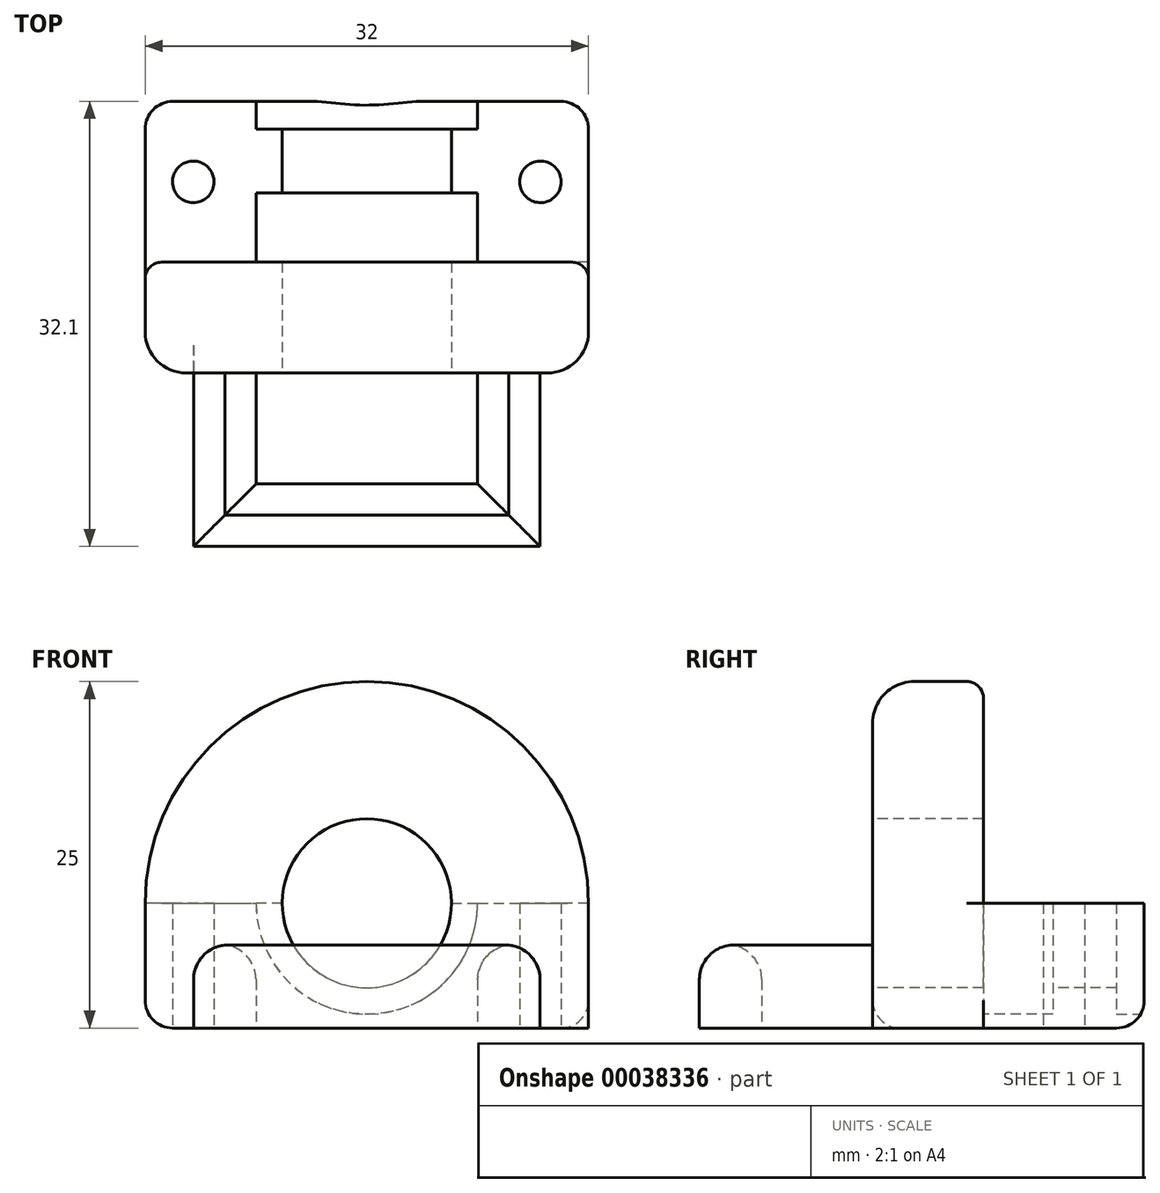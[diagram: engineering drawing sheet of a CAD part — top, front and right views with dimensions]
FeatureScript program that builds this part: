
annotation { "Feature Type Name" : "Feature", "Feature Type Description" : "" }
export const myFeature = defineFeature(function(context is Context, id is Id, definition is map)
    precondition{}
    {
        {
            var Q0;
            Q0=qCreatedBy(makeId("Top.planeOp"),FACE);
            var sketch = newSketch(context, id + "F0", { "sketchPlane" : qUnion([Q0])});
            skLineSegment(sketch, "E0.rect.bottom", {"start": v(-16, 5.8) * mm, "end": v(16, 5.8) * mm});
            skLineSegment(sketch, "E0.rect.top", {"start": v(-16, -5.8) * mm, "end": v(16, -5.8) * mm});
            skLineSegment(sketch, "E0.rect.left", {"start": v(-16, 5.8) * mm, "end": v(-16, -5.8) * mm});
            skLineSegment(sketch, "E0.rect.right", {"start": v(16, 5.8) * mm, "end": v(16, -5.8) * mm});
            skPoint(sketch, "E0.rect.middle", {"position": v(0, 0) * mm});
            skCircle(sketch, "E1", {"center": v(12.52, 0) * mm, "radius": 1.5 * mm});
            skCircle(sketch, "E2", {"center": v(-12.52, 0) * mm, "radius": 1.5 * mm});
            skSolve(sketch);
        }
        {
            var Q0;
            Q0=makeQuery(id+"F0.imprint","IMPRINT",FACE,{"disambiguationData":[TD([[makeQuery(id+"F0.imprint","IMPRINT",EDGE,{"derivedFrom":sQuery(id+"F0.wireOp",EDGE,"E0.rect.bottom")}),-1.0]])]});
            extrude(context, id + "F1", {"entities" : qUnion([Q0]), "depth" : 9 * mm});
        }
        {
            var Q0;
            Q0=makeQuery(id+"F1.opExtrude","SWEPT_FACE",FACE,{"disambiguationData":[OSD([sQuery(id+"F0.wireOp",EDGE,"E0.rect.top")])]});
            var sketch = newSketch(context, id + "F2", { "sketchPlane" : qUnion([Q0])});
            skCircle(sketch, "E3", {"center": v(0, 9) * mm, "radius": 8 * mm});
            skSolve(sketch);
        }
        {
            var Q0;
            Q0=qSketchRegion(id+"F2",true);
            var Q1;
            Q1=makeQuery(id+"F1.opExtrude","SWEPT_FACE",FACE,{"disambiguationData":[OSD([sQuery(id+"F0.wireOp",EDGE,"E0.rect.bottom")])]});
            extrude(context, id + "F3", {"entities" : qUnion([Q0, Q1]), "operationType" : NewBodyOperationType.REMOVE, "oppositeDirection" : true, "depth" : 5 * mm});
        }
        {
            var Q0;
            Q0=makeQuery(id+"F1.opExtrude","SWEPT_FACE",FACE,{"disambiguationData":[OSD([sQuery(id+"F0.wireOp",EDGE,"E0.rect.bottom")])]});
            var sketch = newSketch(context, id + "F4", { "sketchPlane" : qUnion([Q0])});
            skCircle(sketch, "E4", {"center": v(0, 9) * mm, "radius": 8 * mm});
            skSolve(sketch);
        }
        {
            var Q0;
            Q0=qSketchRegion(id+"F4",true);
            extrude(context, id + "F5", {"entities" : qUnion([Q0]), "operationType" : NewBodyOperationType.REMOVE, "oppositeDirection" : true, "depth" : 2 * mm});
        }
        {
            var Q0;
            Q0=makeQuery(id+"F5.boolean.opBoolean","COPY",FACE,{"derivedFrom":makeQuery(id+"F5.opExtrude","CAP_FACE",FACE,{"disambiguationData":[OSD([sQuery(id+"F4.wireOp",EDGE,"E4")])],"isStart":false})});
            var sketch = newSketch(context, id + "F6", { "sketchPlane" : qUnion([Q0])});
            skCircle(sketch, "E5", {"center": v(0, 9) * mm, "radius": 6 * mm});
            skSolve(sketch);
        }
        {
            var Q0;
            Q0=qSketchRegion(id+"F6",true);
            extrude(context, id + "F7", {"entities" : qUnion([Q0]), "operationType" : NewBodyOperationType.REMOVE, "oppositeDirection" : true, "depth" : 25 * mm});
        }
        {
            var Q0;
            Q0=makeQuery(id+"F1.opExtrude","CAP_EDGE",EDGE,{"disambiguationData":[OSD([sQuery(id+"F0.wireOp",EDGE,"E0.rect.bottom")])],"isStart":true});
            var Q1;
            Q1=makeQuery(id+"F7.boolean.opBoolean","COPY",EDGE,{"derivedFrom":makeQuery(id+"F7.opExtrude","CAP_EDGE",EDGE,{"disambiguationData":[OSD([sQuery(id+"F6.wireOp",EDGE,"E5")])],"isStart":true})});
            var Q2;
            Q2=makeQuery(id+"F1.opExtrude","SWEPT_EDGE",EDGE,{"disambiguationData":[OSD([sQuery(id+"F0.wireOp",EDGE,"E0.rect.bottom"),sQuery(id+"F0.wireOp",EDGE,"E0.rect.left")])]});
            var Q3;
            Q3=makeQuery(id+"F1.opExtrude","CAP_EDGE",EDGE,{"disambiguationData":[OSD([sQuery(id+"F0.wireOp",EDGE,"E0.rect.left")])],"isStart":true});
            var Q4;
            Q4=makeQuery(id+"F1.opExtrude","CAP_EDGE",EDGE,{"disambiguationData":[OSD([sQuery(id+"F0.wireOp",EDGE,"E0.rect.right")])],"isStart":true});
            var Q5;
            Q5=makeQuery(id+"F1.opExtrude","SWEPT_EDGE",EDGE,{"disambiguationData":[OSD([sQuery(id+"F0.wireOp",EDGE,"E0.rect.bottom"),sQuery(id+"F0.wireOp",EDGE,"E0.rect.right")])]});
            fillet(context, id + "F8", {"entities" : qUnion([Q0, Q1, Q2, Q3, Q4, Q5]), "radius" : 2 * mm, "tangentPropagation" : true, "allowEdgeOverflow" : false});
        }
        {
            var Q0;
            Q0=makeQuery(id+"F1.opExtrude","SWEPT_FACE",FACE,{"disambiguationData":[OSD([sQuery(id+"F0.wireOp",EDGE,"E0.rect.top")])]});
            var sketch = newSketch(context, id + "F9", { "sketchPlane" : qUnion([Q0])});
            skArc(sketch, "E6", {"start": v(16, 9) * mm, "mid": v(0, 25) * mm, "end": v(-16, 9) * mm});
            skLineSegment(sketch, "E7", {"start": v(0, 0) * mm, "end": v(13.23, 0) * mm});
            skLineSegment(sketch, "E8", {"start": v(-13.23, 0) * mm, "end": v(0, 0) * mm});
            skLineSegment(sketch, "E9", {"start": v(-16, 9) * mm, "end": v(-16, 0) * mm});
            skLineSegment(sketch, "E10", {"start": v(16, 9) * mm, "end": v(16, 0) * mm});
            skLineSegment(sketch, "E11", {"start": v(-16, 0) * mm, "end": v(16, 0) * mm});
            skSolve(sketch);
        }
        {
            var Q0;
            Q0=qSketchRegion(id+"F9",true);
            extrude(context, id + "F10", {"entities" : qUnion([Q0]), "operationType" : NewBodyOperationType.ADD, "depth" : 8 * mm});
        }
        {
            var Q0;
            Q0=qCreatedBy(makeId("Top.planeOp"),FACE);
            var sketch = newSketch(context, id + "F11", { "sketchPlane" : qUnion([Q0])});
            skLineSegment(sketch, "E12", {"start": v(-8, -13.8) * mm, "end": v(-12.5, -13.8) * mm});
            skLineSegment(sketch, "E13", {"start": v(-12.5, -13.8) * mm, "end": v(-8, -13.8) * mm});
            skLineSegment(sketch, "E14", {"start": v(12.5, -13.8) * mm, "end": v(12.5, -26.3) * mm});
            skLineSegment(sketch, "E15", {"start": v(12.5, -26.3) * mm, "end": v(-12.5, -26.3) * mm});
            skLineSegment(sketch, "E16", {"start": v(-12.5, -26.3) * mm, "end": v(-12.5, -13.8) * mm});
            skLineSegment(sketch, "E17", {"start": v(-8, -13.8) * mm, "end": v(-8, -21.8) * mm});
            skLineSegment(sketch, "E18", {"start": v(-8, -21.8) * mm, "end": v(8, -21.8) * mm});
            skLineSegment(sketch, "E19", {"start": v(8, -21.8) * mm, "end": v(8, -13.8) * mm});
            skLineSegment(sketch, "E20.trimOffspring", {"start": v(8, -13.8) * mm, "end": v(12.5, -13.8) * mm});
            skPoint(sketch, "E21.orphan", {"position": v(0, -13.8) * mm});
            skPoint(sketch, "E22", {"position": v(0, -21.8) * mm});
            skPoint(sketch, "E23", {"position": v(0, -26.3) * mm});
            skSolve(sketch);
        }
        {
            var Q0;
            Q0=qSketchRegion(id+"F11",true);
            extrude(context, id + "F12", {"entities" : qUnion([Q0]), "operationType" : NewBodyOperationType.ADD, "depth" : 6 * mm});
        }
        {
            var Q0;
            Q0=makeQuery(id+"F12.opExtrude","CAP_EDGE",EDGE,{"disambiguationData":[OSD([sQuery(id+"F11.wireOp",EDGE,"E17")])],"isStart":false});
            var Q1;
            Q1=makeQuery(id+"F12.opExtrude","CAP_EDGE",EDGE,{"disambiguationData":[OSD([sQuery(id+"F11.wireOp",EDGE,"E16")])],"isStart":false});
            var Q2;
            Q2=makeQuery(id+"F12.opExtrude","CAP_EDGE",EDGE,{"disambiguationData":[OSD([sQuery(id+"F11.wireOp",EDGE,"E19")])],"isStart":false});
            var Q3;
            Q3=makeQuery(id+"F12.opExtrude","CAP_EDGE",EDGE,{"disambiguationData":[OSD([sQuery(id+"F11.wireOp",EDGE,"E14")])],"isStart":false});
            var Q4;
            Q4=makeQuery(id+"F12.opExtrude","CAP_EDGE",EDGE,{"disambiguationData":[OSD([sQuery(id+"F11.wireOp",EDGE,"E18")])],"isStart":false});
            var Q5;
            Q5=makeQuery(id+"F12.opExtrude","CAP_EDGE",EDGE,{"disambiguationData":[OSD([sQuery(id+"F11.wireOp",EDGE,"E15")])],"isStart":false});
            fillet(context, id + "F13", {"entities" : qUnion([Q0, Q1, Q2, Q3, Q4, Q5]), "radius" : 2.5 * mm, "tangentPropagation" : true, "allowEdgeOverflow" : false});
        }
        {
            var Q0;
            Q0=makeQuery(id+"F10.opExtrude","CAP_EDGE",EDGE,{"disambiguationData":[OSD([sQuery(id+"F9.wireOp",EDGE,"E6")])],"isStart":false});
            fillet(context, id + "F14", {"entities" : qUnion([Q0]), "radius" : 3 * mm, "tangentPropagation" : true, "allowEdgeOverflow" : false});
        }
        {
            var Q0;
            Q0=makeQuery(id+"F10.opExtrude","CAP_EDGE",EDGE,{"disambiguationData":[OSD([sQuery(id+"F9.wireOp",EDGE,"E6")])],"isStart":true});
            fillet(context, id + "F15", {"entities" : qUnion([Q0]), "radius" : 1.2 * mm, "tangentPropagation" : true, "allowEdgeOverflow" : false});
        }
        {
            var Q0;
            Q0=makeQuery(id+"F10.opExtrude","CAP_FACE",FACE,{"disambiguationData":[OSD([sQuery(id+"F9.wireOp",EDGE,"E6"),sQuery(id+"F9.wireOp",EDGE,"E9"),sQuery(id+"F9.wireOp",EDGE,"E10"),sQuery(id+"F9.wireOp",EDGE,"E11")])],"isStart":false});
            var sketch = newSketch(context, id + "F16", { "sketchPlane" : qUnion([Q0])});
            skCircle(sketch, "E24", {"center": v(0, 9) * mm, "radius": 6.1 * mm});
            skSolve(sketch);
        }
        {
            var Q0;
            Q0=qSketchRegion(id+"F16",true);
            extrude(context, id + "F17", {"entities" : qUnion([Q0]), "operationType" : NewBodyOperationType.REMOVE, "endBound" : BoundingType.THROUGH_ALL, "oppositeDirection" : true, "depth" : 25 * mm});
        }
        {
            var Q0;
            Q0=makeQuery(id+"F14.opFillet","BLEND_EDGE",EDGE,{"blendedFrom":[makeQuery(id+"F10.opExtrude","CAP_EDGE",EDGE,{"disambiguationData":[OSD([sQuery(id+"F9.wireOp",EDGE,"E9")])],"isStart":false}),makeQuery(id+"F10.boolean.opBoolean","MERGE",FACE,{"derivedFrom":[makeQuery(id+"F1.opExtrude","CAP_FACE",FACE,{"disambiguationData":[OSD([sQuery(id+"F0.wireOp",EDGE,"E0.rect.bottom"),sQuery(id+"F0.wireOp",EDGE,"E0.rect.top"),sQuery(id+"F0.wireOp",EDGE,"E0.rect.left"),sQuery(id+"F0.wireOp",EDGE,"E0.rect.right"),sQuery(id+"F0.wireOp",EDGE,"E1"),sQuery(id+"F0.wireOp",EDGE,"E2")])],"isStart":true}),makeQuery(id+"F10.opExtrude","SWEPT_FACE",FACE,{"disambiguationData":[OSD([sQuery(id+"F9.wireOp",EDGE,"E11")])]})]})],"blendedInto":[makeQuery(id+"F10.boolean.opBoolean","MERGE",FACE,{"derivedFrom":[makeQuery(id+"F1.opExtrude","CAP_FACE",FACE,{"disambiguationData":[OSD([sQuery(id+"F0.wireOp",EDGE,"E0.rect.bottom"),sQuery(id+"F0.wireOp",EDGE,"E0.rect.top"),sQuery(id+"F0.wireOp",EDGE,"E0.rect.left"),sQuery(id+"F0.wireOp",EDGE,"E0.rect.right"),sQuery(id+"F0.wireOp",EDGE,"E1"),sQuery(id+"F0.wireOp",EDGE,"E2")])],"isStart":true}),makeQuery(id+"F10.opExtrude","SWEPT_FACE",FACE,{"disambiguationData":[OSD([sQuery(id+"F9.wireOp",EDGE,"E11")])]})]})]});
            fillet(context, id + "F18", {"entities" : qUnion([Q0]), "radius" : 2 * mm, "tangentPropagation" : true, "allowEdgeOverflow" : false});
        }
    });
